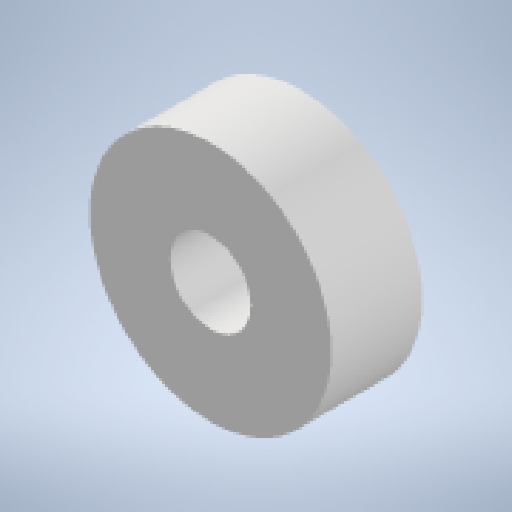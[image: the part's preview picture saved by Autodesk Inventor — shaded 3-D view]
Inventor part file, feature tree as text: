
AUTODESK INVENTOR PART (.ipt)
format: ipt  version: 2023 (Build 270158000, 158)  size: 211,456 bytes
history: native  units: in
note: dims shown in document units (in); Inventor stores cm internally (conversion verified against a paired STEP export)
features: extrude x1, sketch x1
ambient origin geometry x8: Origin, YZ Plane, XZ Plane, XY Plane, X Axis, Y Axis, Z Axis, Center Point
bodies: Solid1 (feature_tree)
feature tree (2):
  extrude  "Extrusion1"  Depth=0.2812in
  sketch  "Sketch1"  dims[d0=0.25in d1=0.747in d2=0.2812in d3=0.0in]
